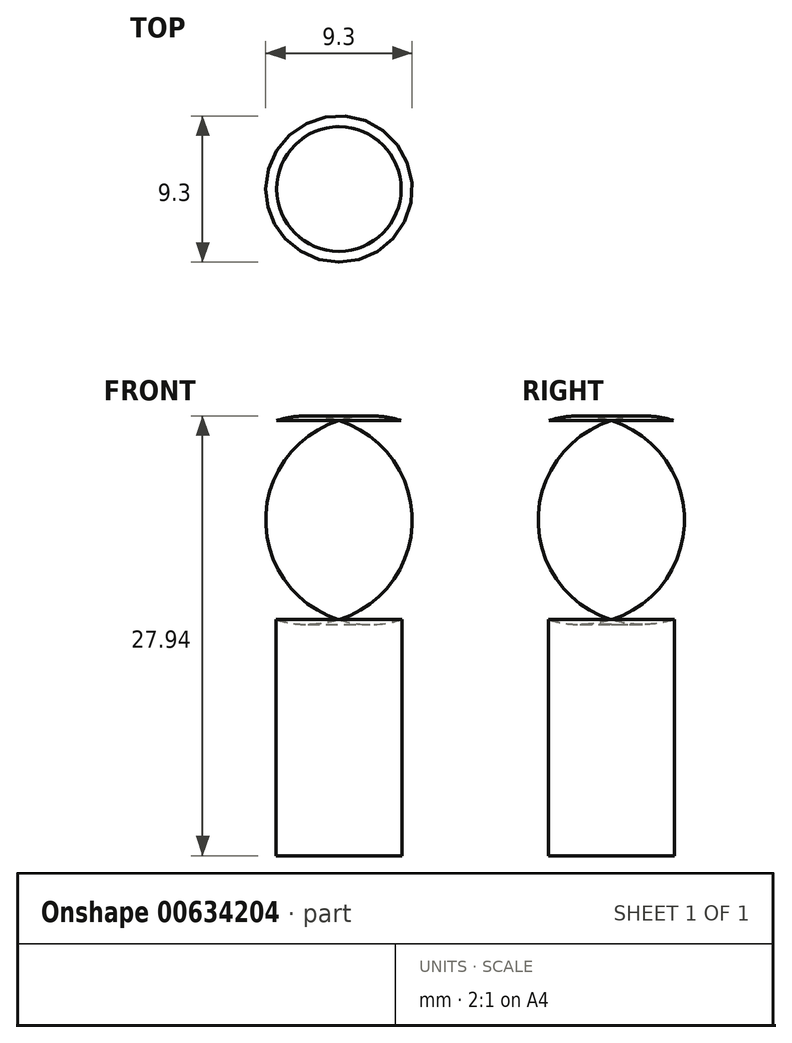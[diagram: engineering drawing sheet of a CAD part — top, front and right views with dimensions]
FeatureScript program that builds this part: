
annotation { "Feature Type Name" : "Feature", "Feature Type Description" : "" }
export const myFeature = defineFeature(function(context is Context, id is Id, definition is map)
    precondition{}
    {
        {
            var Q0;
            Q0=qCreatedBy(makeId("Front.planeOp"),FACE);
            var sketch = newSketch(context, id + "F0", { "sketchPlane" : qUnion([Q0])});
            skLineSegment(sketch, "E0", {"start": v(4, 15) * mm, "end": v(4, 0) * mm});
            skLineSegment(sketch, "E1", {"start": v(0, 53) * mm, "end": v(0, -23.33) * mm, "construction": true});
            skLineSegment(sketch, "E2", {"start": v(4, 0) * mm, "end": v(0, 0) * mm});
            skLineSegment(sketch, "E3", {"start": v(0, 0) * mm, "end": v(0, 27.64) * mm});
            skArc(sketch, "E4", {"start": v(4, 15) * mm, "mid": v(8.6, 21.33) * mm, "end": v(3.95, 27.64) * mm});
            skLineSegment(sketch, "E5", {"start": v(0, 27.64) * mm, "end": v(3.95, 27.64) * mm});
            skSolve(sketch);
        }
        {
            var Q0;
            Q0 = qSketchRegion(id + "F0", true);
            var Q1;
            Q1=sQuery(id+"F0.wireOp",EDGE,"E1");
            revolve(context, id + "F1", {"entities" : qUnion([Q0]), "axis" : qUnion([Q1]), "revolveType" : RevolveType.FULL});
        }
    });
